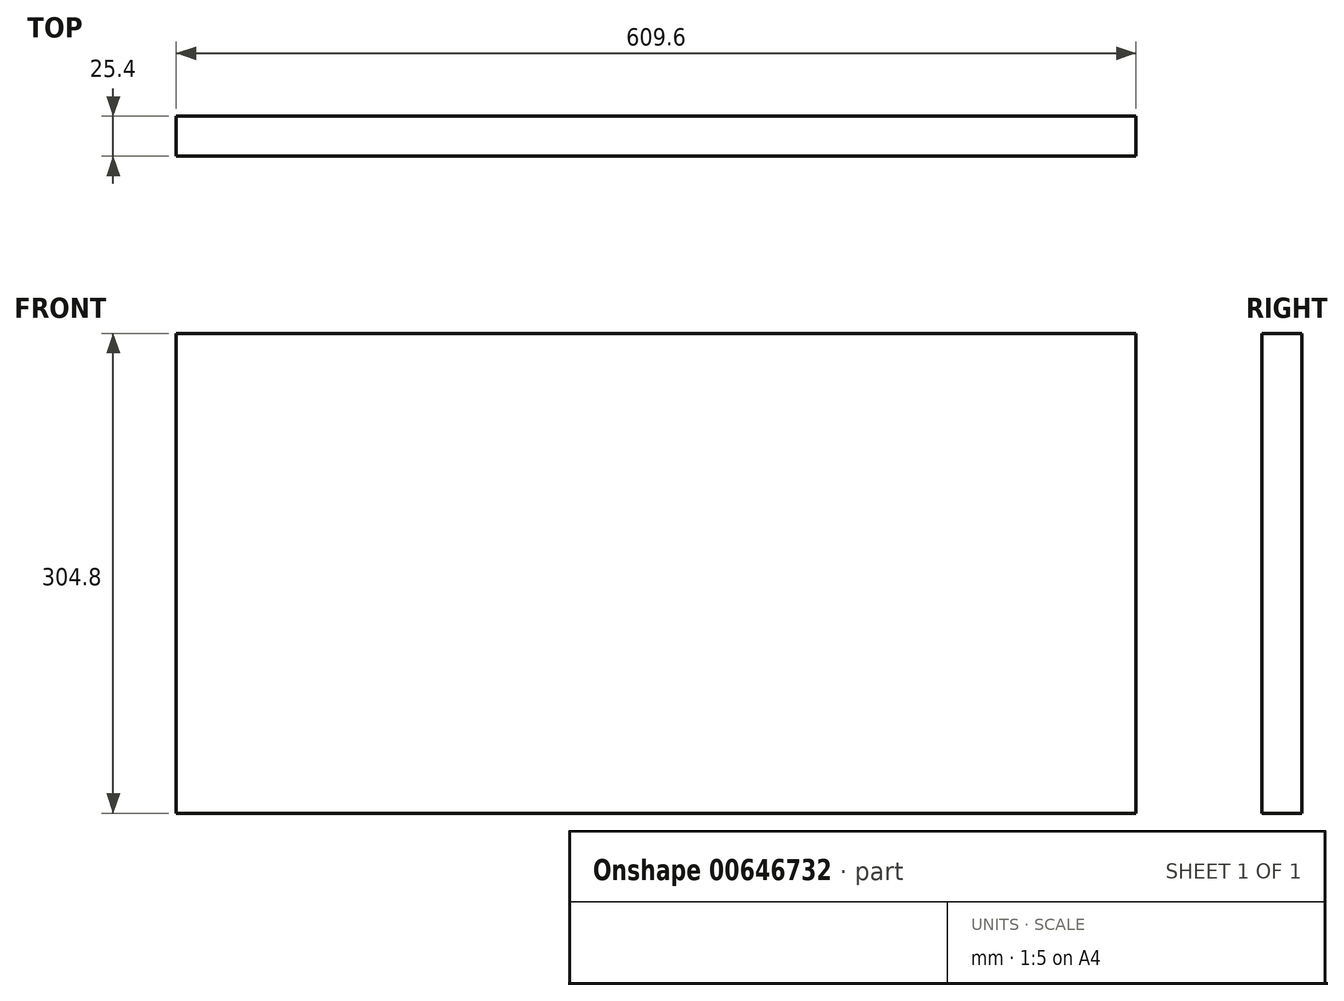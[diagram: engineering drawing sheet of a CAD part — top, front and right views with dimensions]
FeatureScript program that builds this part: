
annotation { "Feature Type Name" : "Feature", "Feature Type Description" : "" }
export const myFeature = defineFeature(function(context is Context, id is Id, definition is map)
    precondition{}
    {
        {
            var Q0;
            Q0=qCreatedBy(makeId("Front.planeOp"),FACE);
            var sketch = newSketch(context, id + "F0", { "sketchPlane" : qUnion([Q0])});
            skLineSegment(sketch, "E0.bottom", {"start": v(-66.05, 240.19) * mm, "end": v(543.55, 240.19) * mm});
            skLineSegment(sketch, "E0.top", {"start": v(-66.05, -64.61) * mm, "end": v(543.55, -64.61) * mm});
            skLineSegment(sketch, "E0.left", {"start": v(-66.05, 240.19) * mm, "end": v(-66.05, -64.61) * mm});
            skLineSegment(sketch, "E0.right", {"start": v(543.55, 240.19) * mm, "end": v(543.55, -64.61) * mm});
            skSolve(sketch);
        }
        {
            var Q0;
            Q0=makeQuery(id+"F0.imprint","IMPRINT",FACE,{"disambiguationData":[TD([[makeQuery(id+"F0.imprint","IMPRINT",EDGE,{"derivedFrom":sQuery(id+"F0.wireOp",EDGE,"E0.bottom")}),-1.0]])]});
            extrude(context, id + "F1", {"entities" : qUnion([Q0]), "depth" : 25.4 * mm, "offsetDistance" : 25.4 * mm});
        }
    });
